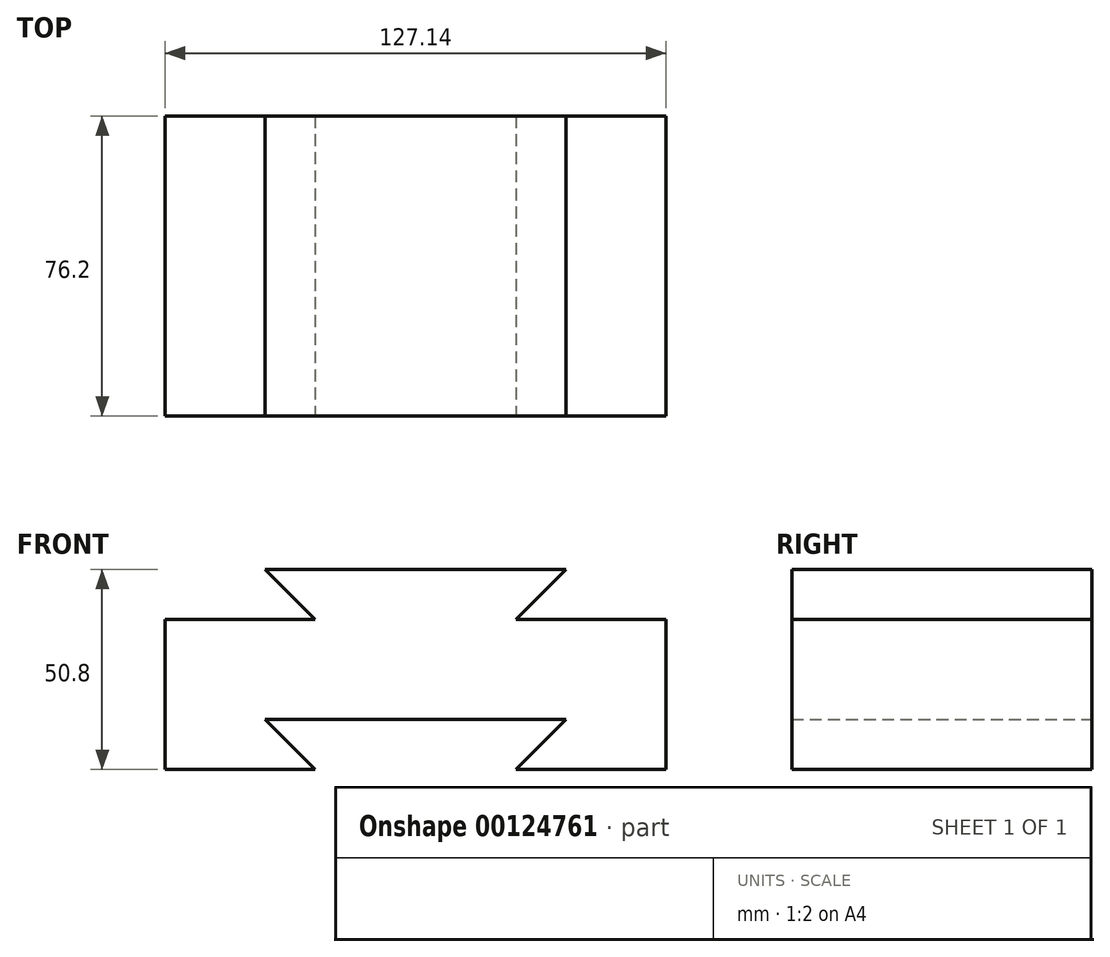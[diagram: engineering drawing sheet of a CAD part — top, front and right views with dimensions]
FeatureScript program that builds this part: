
annotation { "Feature Type Name" : "Feature", "Feature Type Description" : "" }
export const myFeature = defineFeature(function(context is Context, id is Id, definition is map)
    precondition{}
    {
        {
            var Q0;
            Q0=qCreatedBy(makeId("Top.planeOp"),FACE);
            var sketch = newSketch(context, id + "F0", { "sketchPlane" : qUnion([Q0])});
            skLineSegment(sketch, "E0.bottom", {"start": v(-63.57, 38.93) * mm, "end": v(-25.47, 38.93) * mm});
            skLineSegment(sketch, "E0.top", {"start": v(-63.57, -37.27) * mm, "end": v(-25.47, -37.27) * mm});
            skLineSegment(sketch, "E0.left", {"start": v(-63.57, 38.93) * mm, "end": v(-63.57, -37.27) * mm});
            skLineSegment(sketch, "E0.right", {"start": v(-25.47, 38.93) * mm, "end": v(-25.47, -37.27) * mm});
            skSolve(sketch);
        }
        {
            var Q0;
            Q0=makeQuery(id+"F0.imprint","IMPRINT",FACE,{"disambiguationData":[TD([[makeQuery(id+"F0.imprint","IMPRINT",EDGE,{"derivedFrom":sQuery(id+"F0.wireOp",EDGE,"E0.bottom")}),-1.0]])]});
            extrude(context, id + "F1", {"entities" : qUnion([Q0]), "depth" : 12.7 * mm});
        }
        {
            var Q0;
            Q0=makeQuery(id+"F1.opExtrude","CAP_EDGE",EDGE,{"disambiguationData":[OSD([sQuery(id+"F0.wireOp",EDGE,"E0.right")])],"isStart":false});
            chamfer(context, id + "F2", {"entities" : qUnion([Q0]), "width" : 12.7 * mm, "tangentPropagation" : true});
        }
        {
            var Q0;
            Q0=makeQuery(id+"F1.opExtrude","CAP_FACE",FACE,{"disambiguationData":[OSD([sQuery(id+"F0.wireOp",EDGE,"E0.bottom"),sQuery(id+"F0.wireOp",EDGE,"E0.top"),sQuery(id+"F0.wireOp",EDGE,"E0.left"),sQuery(id+"F0.wireOp",EDGE,"E0.right")])],"isStart":false});
            var sketch = newSketch(context, id + "F3", { "sketchPlane" : qUnion([Q0])});
            skLineSegment(sketch, "E1.bottom", {"start": v(-63.57, 38.93) * mm, "end": v(12.63, 38.93) * mm});
            skLineSegment(sketch, "E1.top", {"start": v(-63.57, -37.27) * mm, "end": v(12.63, -37.27) * mm});
            skLineSegment(sketch, "E1.left", {"start": v(-63.57, 38.93) * mm, "end": v(-63.57, -37.27) * mm});
            skLineSegment(sketch, "E1.right", {"start": v(12.63, 38.93) * mm, "end": v(12.63, -37.27) * mm});
            skSolve(sketch);
        }
        {
            var Q0;
            Q0 = qSketchRegion(id + "F3", true);
            extrude(context, id + "F4", {"entities" : qUnion([Q0]), "operationType" : NewBodyOperationType.ADD, "depth" : 25.4 * mm});
        }
        {
            var Q0;
            Q0=makeQuery(id+"F4.opExtrude","CAP_FACE",FACE,{"disambiguationData":[OSD([sQuery(id+"F3.wireOp",EDGE,"E1.bottom"),sQuery(id+"F3.wireOp",EDGE,"E1.top"),sQuery(id+"F3.wireOp",EDGE,"E1.left"),sQuery(id+"F3.wireOp",EDGE,"E1.right")])],"isStart":false});
            var sketch = newSketch(context, id + "F5", { "sketchPlane" : qUnion([Q0])});
            skLineSegment(sketch, "E2.bottom", {"start": v(12.63, 38.93) * mm, "end": v(-38.17, 38.93) * mm});
            skLineSegment(sketch, "E2.top", {"start": v(12.63, -37.27) * mm, "end": v(-38.17, -37.27) * mm});
            skLineSegment(sketch, "E2.left", {"start": v(12.63, 38.93) * mm, "end": v(12.63, -37.27) * mm});
            skLineSegment(sketch, "E2.right", {"start": v(-38.17, 38.93) * mm, "end": v(-38.17, -37.27) * mm});
            skSolve(sketch);
        }
        {
            var Q0;
            Q0=makeQuery(id+"F5.imprint","IMPRINT",FACE,{"disambiguationData":[TD([[makeQuery(id+"F5.imprint","IMPRINT",EDGE,{"derivedFrom":sQuery(id+"F5.wireOp",EDGE,"E2.bottom")}),-1.0]])]});
            extrude(context, id + "F6", {"entities" : qUnion([Q0]), "operationType" : NewBodyOperationType.ADD, "depth" : 12.7 * mm});
        }
        {
            var Q0;
            {var subQ0=makeQuery(id+"F6.boolean.opBoolean","MERGE",FACE,{"derivedFrom":[makeQuery(id+"F4.boolean.opBoolean","MERGE",FACE,{"derivedFrom":[makeQuery(id+"F1.opExtrude","SWEPT_FACE",FACE,{"disambiguationData":[OSD([sQuery(id+"F0.wireOp",EDGE,"E0.top")])]}),makeQuery(id+"F4.opExtrude","SWEPT_FACE",FACE,{"disambiguationData":[OSD([sQuery(id+"F3.wireOp",EDGE,"E1.top")])]})]}),makeQuery(id+"F6.opExtrude","SWEPT_FACE",FACE,{"disambiguationData":[OSD([sQuery(id+"F5.wireOp",EDGE,"E2.top")])]})]});Q0=makeQuery(id+"FDRwq5J7zFCrLcS_1.boolean.opBoolean","MERGE",FACE,{"derivedFrom":[subQ0,makeQuery(id+"FDRwq5J7zFCrLcS_1.opPattern","COPY",FACE,{"derivedFrom":subQ0,"instanceName":"1"})]});}
            var sketch = newSketch(context, id + "F7", { "sketchPlane" : qUnion([Q0])});
            skLineSegment(sketch, "E3", {"start": v(-63.57, 38.1) * mm, "end": v(-25.47, 38.1) * mm});
            skLineSegment(sketch, "E4", {"start": v(-25.47, 38.1) * mm, "end": v(-38.17, 50.8) * mm});
            skSolve(sketch);
        }
        {
            var Q0;
            {var subQ2=sQuery(id+"F7.wireOp",EDGE,"E4");Q0=makeQuery(id+"F7.imprint","IMPRINT",FACE,{"disambiguationData":[TD([[makeQuery(id+"F7.imprint","IMPRINT",EDGE,{"derivedFrom":subQ2}),1.0]])]});}
            extrude(context, id + "F8", {"entities" : qUnion([Q0]), "operationType" : NewBodyOperationType.REMOVE, "endBound" : BoundingType.THROUGH_ALL, "oppositeDirection" : true, "depth" : 25.4 * mm});
        }
        {
            var Q0;
            Q0=makeQuery(id+"F1.opExtrude","SWEPT_BODY",BODY,{"disambiguationData":[OSD([sQuery(id+"F0.wireOp",EDGE,"E0.bottom"),sQuery(id+"F0.wireOp",EDGE,"E0.top"),sQuery(id+"F0.wireOp",EDGE,"E0.left"),sQuery(id+"F0.wireOp",EDGE,"E0.right")])]});
            var Q1;
            Q1=qCreatedBy(makeId("Right.planeOp"),FACE);
            mirror(context, id + "F9", {"operationType" : NewBodyOperationType.ADD, "entities" : qUnion([Q0]), "mirrorPlane" : qUnion([Q1])});
        }
    });
